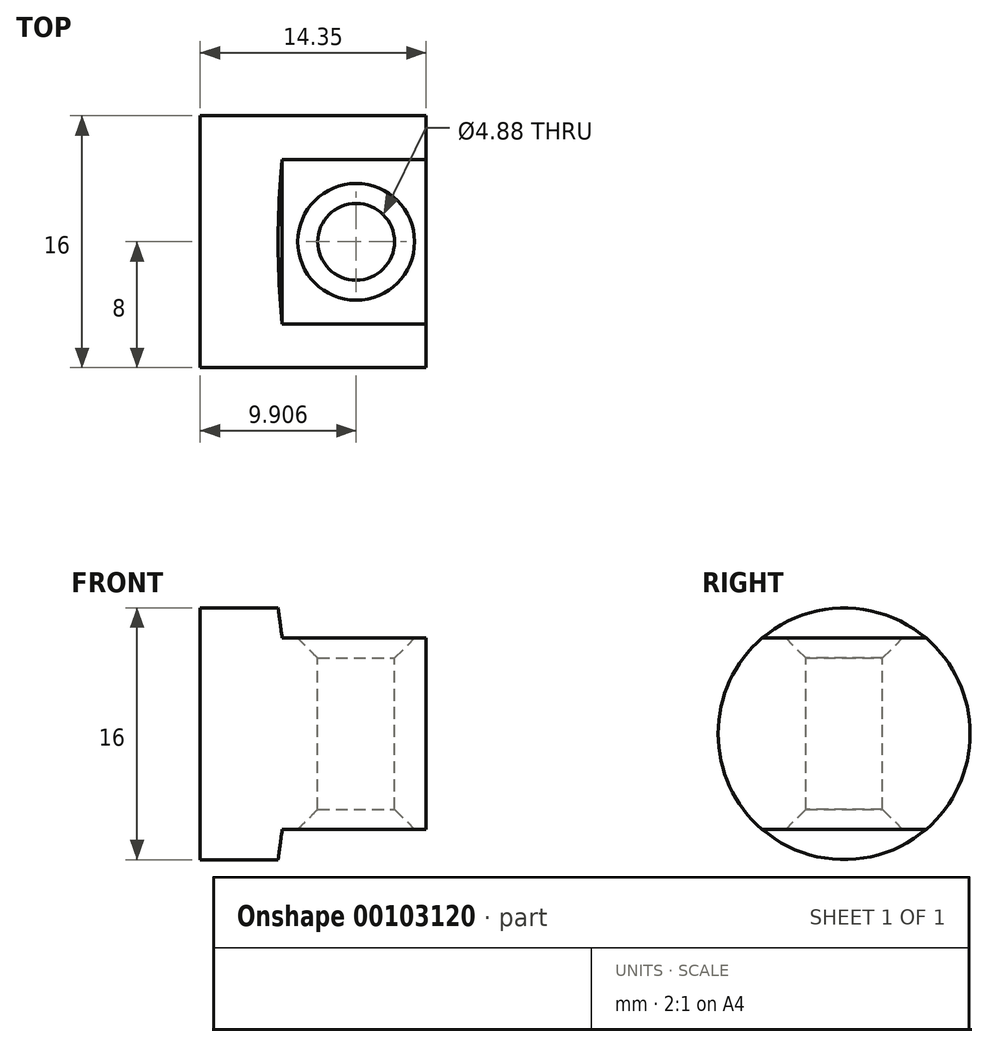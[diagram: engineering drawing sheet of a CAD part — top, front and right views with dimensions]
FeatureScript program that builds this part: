
annotation { "Feature Type Name" : "Feature", "Feature Type Description" : "" }
export const myFeature = defineFeature(function(context is Context, id is Id, definition is map)
    precondition{}
    {
        {
            var Q0;
            Q0=qCreatedBy(makeId("Right.planeOp"),FACE);
            var sketch = newSketch(context, id + "F0", { "sketchPlane" : qUnion([Q0])});
            skCircle(sketch, "E0", {"center": v(0, 0) * mm, "radius": 8 * mm});
            skSolve(sketch);
        }
        {
            var Q0;
            Q0 = qSketchRegion(id + "F0", true);
            extrude(context, id + "F1", {"entities" : qUnion([Q0]), "depth" : 14.35 * mm});
        }
        {
            var Q0;
            Q0=qCreatedBy(makeId("Front.planeOp"),FACE);
            var sketch = newSketch(context, id + "F2", { "sketchPlane" : qUnion([Q0])});
            skLineSegment(sketch, "E1", {"start": v(4.95, 8) * mm, "end": v(5.2, 6.07) * mm});
            skLineSegment(sketch, "E2", {"start": v(5.2, 6.07) * mm, "end": v(14.35, 6.07) * mm});
            skLineSegment(sketch, "E3", {"start": v(14.35, 6.07) * mm, "end": v(14.35, 8) * mm});
            skLineSegment(sketch, "E4", {"start": v(14.35, 8) * mm, "end": v(4.95, 8) * mm});
            skLineSegment(sketch, "E5", {"start": v(0, 8) * mm, "end": v(14.35, 8) * mm});
            skLineSegment(sketch, "E6", {"start": v(14.35, -8) * mm, "end": v(0, -8) * mm});
            skLineSegment(sketch, "E7.MirrorCS", {"start": v(5.2, -6.07) * mm, "end": v(14.35, -6.07) * mm});
            skLineSegment(sketch, "E8.MirrorCS", {"start": v(14.35, -6.07) * mm, "end": v(14.35, -8) * mm});
            skLineSegment(sketch, "E9.MirrorCS", {"start": v(14.35, -8) * mm, "end": v(4.95, -8) * mm});
            skLineSegment(sketch, "E10.MirrorCS", {"start": v(4.95, -8) * mm, "end": v(5.2, -6.07) * mm});
            skSolve(sketch);
        }
        {
            var Q0;
            Q0 = qSketchRegion(id + "F2", true);
            extrude(context, id + "F3", {"entities" : qUnion([Q0]), "operationType" : NewBodyOperationType.REMOVE, "oppositeDirection" : true, "depth" : 25.4 * mm, "hasSecondDirection" : true, "secondDirectionOppositeDirection" : false, "secondDirectionDepth" : 25.4 * mm});
        }
        {
            var Q0;
            Q0=qCreatedBy(makeId("Top.planeOp"),FACE);
            var sketch = newSketch(context, id + "F4", { "sketchPlane" : qUnion([Q0])});
            skCircle(sketch, "E11", {"center": v(9.9, 0) * mm, "radius": 2.44 * mm});
            skSolve(sketch);
        }
        {
            var Q0;
            Q0 = qSketchRegion(id + "F4", true);
            extrude(context, id + "F5", {"entities" : qUnion([Q0]), "operationType" : NewBodyOperationType.REMOVE, "oppositeDirection" : true, "depth" : 25.4 * mm, "hasSecondDirection" : true, "secondDirectionOppositeDirection" : false, "secondDirectionDepth" : 25.4 * mm});
        }
        {
            var Q0;
            Q0=makeQuery(id+"F5.boolean.opBoolean","INTERSECT",EDGE,{"derivedFrom":[makeQuery(id+"F3.boolean.opBoolean","COPY",FACE,{"derivedFrom":makeQuery(id+"F3.opExtrude","SWEPT_FACE",FACE,{"disambiguationData":[OSD([sQuery(id+"F2.wireOp",EDGE,"E2")])]})}),makeQuery(id+"F5.opExtrude","SWEPT_FACE",FACE,{"disambiguationData":[OSD([sQuery(id+"F4.wireOp",EDGE,"E11")])]})]});
            var Q1;
            Q1=makeQuery(id+"F5.boolean.opBoolean","INTERSECT",EDGE,{"derivedFrom":[makeQuery(id+"F3.boolean.opBoolean","COPY",FACE,{"derivedFrom":makeQuery(id+"F3.opExtrude","SWEPT_FACE",FACE,{"disambiguationData":[OSD([sQuery(id+"F2.wireOp",EDGE,"E7.MirrorCS")])]})}),makeQuery(id+"F5.opExtrude","SWEPT_FACE",FACE,{"disambiguationData":[OSD([sQuery(id+"F4.wireOp",EDGE,"E11")])]})]});
            chamfer(context, id + "F6", {"entities" : qUnion([Q0, Q1]), "width" : 1.27 * mm, "tangentPropagation" : true});
        }
    });
